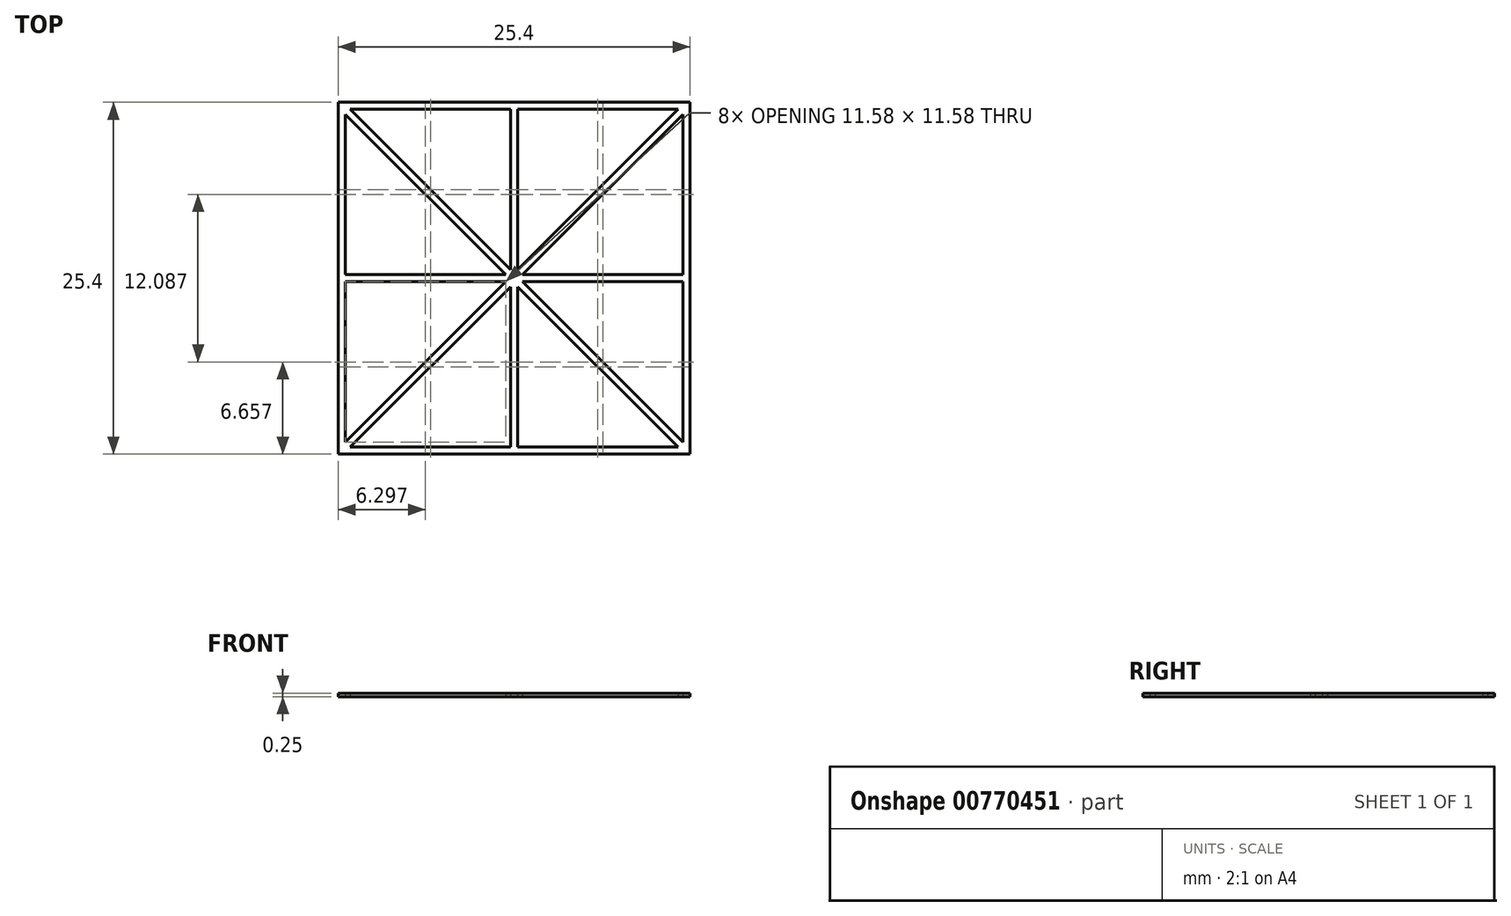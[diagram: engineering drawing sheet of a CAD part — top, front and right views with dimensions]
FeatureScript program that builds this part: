
annotation { "Feature Type Name" : "Feature", "Feature Type Description" : "" }
export const myFeature = defineFeature(function(context is Context, id is Id, definition is map)
    precondition{}
    {
        {
            var Q0;
            Q0=qCreatedBy(makeId("Top.planeOp"),FACE);
            var sketch = newSketch(context, id + "F0", { "sketchPlane" : qUnion([Q0])});
            skLineSegment(sketch, "E0.bottom", {"start": v(-12.7, -12.7) * mm, "end": v(12.7, -12.7) * mm, "construction": true});
            skLineSegment(sketch, "E0.top", {"start": v(-12.7, 12.7) * mm, "end": v(12.7, 12.7) * mm, "construction": true});
            skLineSegment(sketch, "E0.left", {"start": v(-12.7, -12.7) * mm, "end": v(-12.7, 12.7) * mm, "construction": true});
            skLineSegment(sketch, "E0.right", {"start": v(12.7, -12.7) * mm, "end": v(12.7, 12.7) * mm, "construction": true});
            skPoint(sketch, "E0.middle", {"position": v(0, 0) * mm});
            skLineSegment(sketch, "E1.bottom", {"start": v(-12.2, -12.2) * mm, "end": v(12.2, -12.2) * mm, "construction": true});
            skLineSegment(sketch, "E1.top", {"start": v(-12.2, 12.2) * mm, "end": v(12.2, 12.2) * mm, "construction": true});
            skLineSegment(sketch, "E1.left", {"start": v(-12.2, -12.2) * mm, "end": v(-12.2, 12.2) * mm, "construction": true});
            skLineSegment(sketch, "E1.right", {"start": v(12.2, -12.2) * mm, "end": v(12.2, 12.2) * mm, "construction": true});
            skLineSegment(sketch, "E2", {"start": v(0, 0) * mm, "end": v(0, 12.2) * mm, "construction": true});
            skLineSegment(sketch, "E3", {"start": v(-12.2, 12.2) * mm, "end": v(12.2, -12.2) * mm, "construction": true});
            skLineSegment(sketch, "E4", {"start": v(-12.2, -12.2) * mm, "end": v(12.2, 12.2) * mm, "construction": true});
            skLineSegment(sketch, "E5", {"start": v(0, 0) * mm, "end": v(-12.2, 0) * mm, "construction": true});
            skLineSegment(sketch, "E6", {"start": v(-0.25, 12.2) * mm, "end": v(-0.25, -12.2) * mm, "construction": true});
            skLineSegment(sketch, "E7", {"start": v(0.25, 12.2) * mm, "end": v(0.25, -12.2) * mm, "construction": true});
            skLineSegment(sketch, "E8", {"start": v(11.83, 12.2) * mm, "end": v(-12.2, -11.83) * mm, "construction": true});
            skLineSegment(sketch, "E9.0", {"start": v(12.2, 11.83) * mm, "end": v(-11.83, -12.2) * mm, "construction": true});
            skLineSegment(sketch, "E10.0", {"start": v(-12.2, 11.83) * mm, "end": v(11.83, -12.2) * mm, "construction": true});
            skLineSegment(sketch, "E11.0", {"start": v(-11.83, 12.2) * mm, "end": v(12.2, -11.83) * mm, "construction": true});
            skLineSegment(sketch, "E12.0", {"start": v(12.2, 0.25) * mm, "end": v(-12.2, 0.25) * mm, "construction": true});
            skLineSegment(sketch, "E13.0", {"start": v(12.2, -0.25) * mm, "end": v(-12.2, -0.25) * mm, "construction": true});
            skSolve(sketch);
        }
        {
            var Q0;
            Q0=qCreatedBy(makeId("Top.planeOp"),FACE);
            var sketch = newSketch(context, id + "F1", { "sketchPlane" : qUnion([Q0])});
            skPoint(sketch, "E14.middle", {"position": v(0, 0) * mm});
            skLineSegment(sketch, "E15.0", {"start": v(-12.7, 12.7) * mm, "end": v(12.7, 12.7) * mm});
            skLineSegment(sketch, "E16.1", {"start": v(12.7, -12.7) * mm, "end": v(12.7, 12.7) * mm});
            skLineSegment(sketch, "E17.1", {"start": v(-12.7, -12.7) * mm, "end": v(12.7, -12.7) * mm});
            skLineSegment(sketch, "E18.0", {"start": v(-12.7, -12.7) * mm, "end": v(-12.7, 12.7) * mm});
            skLineSegment(sketch, "E19.0", {"start": v(-11.83, 12.2) * mm, "end": v(-0.25, 12.2) * mm});
            skLineSegment(sketch, "E20.0", {"start": v(-0.25, 12.2) * mm, "end": v(-0.25, 0.61) * mm});
            skLineSegment(sketch, "E21.0", {"start": v(0.25, 12.2) * mm, "end": v(0.25, 0.61) * mm});
            skLineSegment(sketch, "E22.0", {"start": v(-12.2, -11.83) * mm, "end": v(-12.2, -0.25) * mm});
            skLineSegment(sketch, "E23.0", {"start": v(-11.83, 12.2) * mm, "end": v(-0.25, 0.61) * mm});
            skLineSegment(sketch, "E24.0", {"start": v(-12.2, 11.83) * mm, "end": v(-0.61, 0.25) * mm});
            skLineSegment(sketch, "E25.0", {"start": v(12.2, -11.83) * mm, "end": v(12.2, -0.25) * mm});
            skLineSegment(sketch, "E26.0", {"start": v(-11.83, -12.2) * mm, "end": v(-0.25, -12.2) * mm});
            skLineSegment(sketch, "E27.0", {"start": v(12.2, 11.83) * mm, "end": v(0.61, 0.25) * mm});
            skLineSegment(sketch, "E28.0", {"start": v(11.83, 12.2) * mm, "end": v(0.25, 0.61) * mm});
            skLineSegment(sketch, "E29.0", {"start": v(12.2, 0.25) * mm, "end": v(0.61, 0.25) * mm});
            skLineSegment(sketch, "E30.0", {"start": v(12.2, -0.25) * mm, "end": v(0.61, -0.25) * mm});
            skLineSegment(sketch, "E31.trimOffspring", {"start": v(0.25, 12.2) * mm, "end": v(11.83, 12.2) * mm});
            skLineSegment(sketch, "E32.trimOffspring", {"start": v(0.25, -12.2) * mm, "end": v(11.83, -12.2) * mm});
            skLineSegment(sketch, "E33.trimOffspring", {"start": v(12.2, 0.25) * mm, "end": v(12.2, 11.83) * mm});
            skLineSegment(sketch, "E34.trimOffspring", {"start": v(-12.2, 0.25) * mm, "end": v(-12.2, 11.83) * mm});
            skLineSegment(sketch, "E35.trimOffspring", {"start": v(-0.61, 0.25) * mm, "end": v(-12.2, 0.25) * mm});
            skLineSegment(sketch, "E36.trimOffspring", {"start": v(0.61, -0.25) * mm, "end": v(12.2, -11.83) * mm});
            skLineSegment(sketch, "E37.trimOffspring", {"start": v(0.25, -0.61) * mm, "end": v(0.25, -12.2) * mm});
            skLineSegment(sketch, "E38.trimOffspring", {"start": v(0.25, -0.61) * mm, "end": v(11.83, -12.2) * mm});
            skLineSegment(sketch, "E39.trimOffspring", {"start": v(-0.25, -0.61) * mm, "end": v(-11.83, -12.2) * mm});
            skLineSegment(sketch, "E40.trimOffspring", {"start": v(-0.61, -0.25) * mm, "end": v(-12.2, -11.83) * mm});
            skLineSegment(sketch, "E41.trimOffspring", {"start": v(-0.61, -0.25) * mm, "end": v(-12.2, -0.25) * mm});
            skLineSegment(sketch, "E42.trimOffspring", {"start": v(-0.25, -0.61) * mm, "end": v(-0.25, -12.2) * mm});
            skPoint(sketch, "E43.orphan", {"position": v(-12.2, 12.2) * mm});
            skPoint(sketch, "E44.orphan", {"position": v(12.2, 12.2) * mm});
            skPoint(sketch, "E45.orphan", {"position": v(12.2, -12.2) * mm});
            skPoint(sketch, "E46.orphan", {"position": v(-12.2, -12.2) * mm});
            skSolve(sketch);
        }
        {
            var Q0;
            Q0 = qSketchRegion(id + "F1", true);
            extrude(context, id + "F2", {"entities" : qUnion([Q0]), "depth" : 0.25 * mm, "offsetDistance" : 25.4 * mm});
        }
    });
